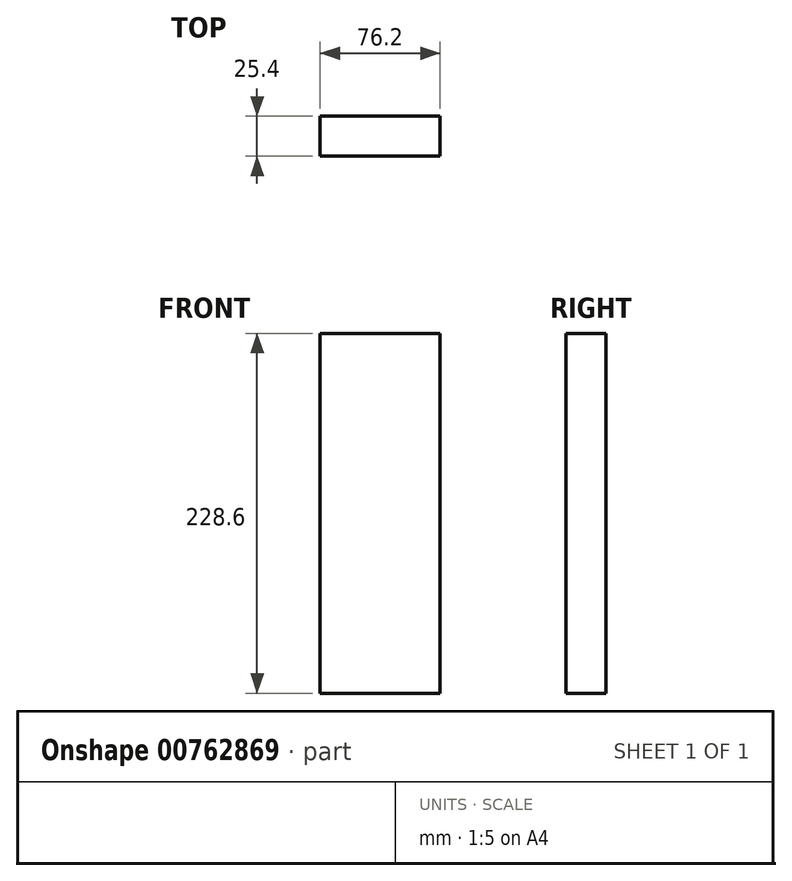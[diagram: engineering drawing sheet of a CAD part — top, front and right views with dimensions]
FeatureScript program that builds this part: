
annotation { "Feature Type Name" : "Feature", "Feature Type Description" : "" }
export const myFeature = defineFeature(function(context is Context, id is Id, definition is map)
    precondition{}
    {
        {
            var Q0;
            Q0=qCreatedBy(makeId("Front.planeOp"),FACE);
            var sketch = newSketch(context, id + "F0", { "sketchPlane" : qUnion([Q0])});
            skLineSegment(sketch, "E0.bottom", {"start": v(0, 0) * mm, "end": v(76.2, 0) * mm});
            skLineSegment(sketch, "E0.top", {"start": v(0, 228.6) * mm, "end": v(76.2, 228.6) * mm});
            skLineSegment(sketch, "E0.left", {"start": v(0, 0) * mm, "end": v(0, 228.6) * mm});
            skLineSegment(sketch, "E0.right", {"start": v(76.2, 0) * mm, "end": v(76.2, 228.6) * mm});
            skSolve(sketch);
        }
        {
            var Q0;
            Q0 = qSketchRegion(id + "F0", true);
            extrude(context, id + "F1", {"entities" : qUnion([Q0]), "depth" : 25.4 * mm, "offsetDistance" : 25.4 * mm});
        }
    });
